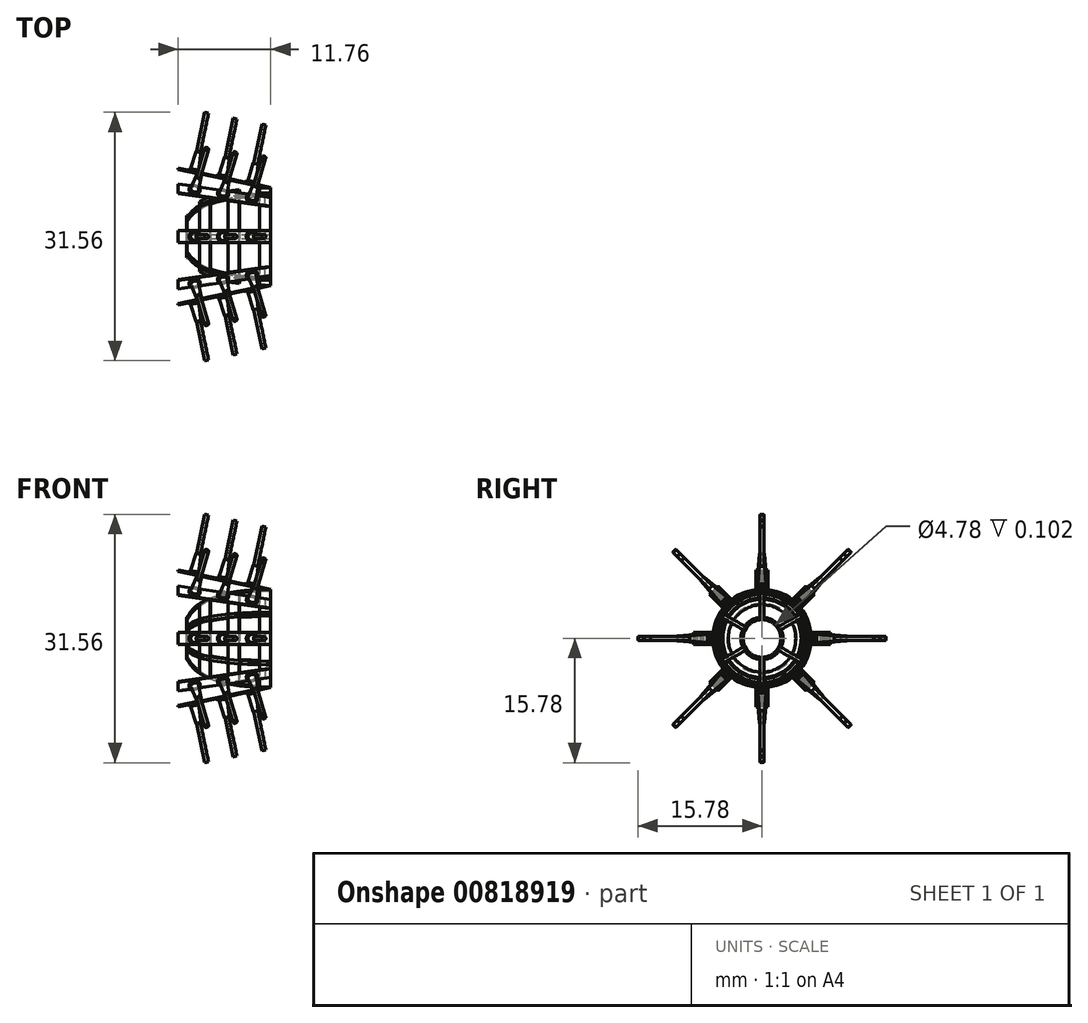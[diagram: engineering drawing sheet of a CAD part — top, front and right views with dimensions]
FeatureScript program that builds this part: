
annotation { "Feature Type Name" : "Feature", "Feature Type Description" : "" }
export const myFeature = defineFeature(function(context is Context, id is Id, definition is map)
    precondition{}
    {
        {
            var Q0;
            Q0=qCreatedBy(makeId("Front.planeOp"),FACE);
            var sketch = newSketch(context, id + "F0", { "sketchPlane" : qUnion([Q0])});
            skFitSpline(sketch, "E0", {"points": [v(0, 2.69) * mm, v(10.6, 6.24) * mm], "startDerivative": vector(4.14, 8.52) * mm, "endDerivative": vector(13.82, 0.2) * mm});
            skFitSpline(sketch, "E1", {"points": [v(0, 2.38) * mm, v(10.6, 6.06) * mm], "startDerivative": vector(4.46, 8.98) * mm, "endDerivative": vector(13.82, 0.2) * mm});
            skLineSegment(sketch, "E2", {"start": v(0, 2.69) * mm, "end": v(0, 2.38) * mm});
            skLineSegment(sketch, "E3", {"start": v(10.6, 6.24) * mm, "end": v(10.6, 6.06) * mm});
            skLineSegment(sketch, "E4", {"start": v(0, -2.69) * mm, "end": v(0, -2.38) * mm});
            skLineSegment(sketch, "E5.MirrorCS", {"start": v(10.6, -6.24) * mm, "end": v(10.6, -6.06) * mm});
            skFitSpline(sketch, "E6.MirrorCS", {"points": [v(0, -2.38) * mm, v(10.6, -6.06) * mm], "startDerivative": vector(4.46, -8.98) * mm, "endDerivative": vector(13.82, -0.2) * mm});
            skFitSpline(sketch, "E7.MirrorCS", {"points": [v(0, -2.69) * mm, v(10.6, -6.24) * mm], "startDerivative": vector(4.14, -8.52) * mm, "endDerivative": vector(13.82, -0.2) * mm});
            skLineSegment(sketch, "E8", {"start": v(0, 0) * mm, "end": v(12.51, 0) * mm, "construction": true});
            skSolve(sketch);
        }
        {
            var Q0;
            Q0=makeQuery(id+"F0.imprint","IMPRINT",FACE,{"disambiguationData":[TD([[makeQuery(id+"F0.imprint","IMPRINT",EDGE,{"derivedFrom":sQuery(id+"F0.wireOp",EDGE,"E0")}),-1.0]])]});
            var Q1;
            Q1=makeQuery(id+"F0.imprint","IMPRINT",FACE,{"disambiguationData":[TD([[makeQuery(id+"F0.imprint","IMPRINT",EDGE,{"derivedFrom":sQuery(id+"F0.wireOp",EDGE,"E4")}),-1.0]])]});
            extrude(context, id + "F1", {"entities" : qUnion([Q0, Q1]), "endBound" : BoundingType.SYMMETRIC, "depth" : 0.5 * mm, "offsetDistance" : 25.4 * mm});
        }
        {
            var Q0;
            Q0=qCreatedBy(makeId("Front.planeOp"),FACE);
            var sketch = newSketch(context, id + "F2", { "sketchPlane" : qUnion([Q0])});
            skLineSegment(sketch, "E9.bottom", {"start": v(0, 2.4) * mm, "end": v(-0.1, 2.4) * mm});
            skLineSegment(sketch, "E9.top", {"start": v(0, 2.68) * mm, "end": v(-0.1, 2.68) * mm});
            skLineSegment(sketch, "E9.left", {"start": v(0, 2.4) * mm, "end": v(0, 2.68) * mm});
            skLineSegment(sketch, "E9.right", {"start": v(-0.1, 2.4) * mm, "end": v(-0.1, 2.68) * mm});
            skLineSegment(sketch, "E10", {"start": v(0.05, 0) * mm, "end": v(4.12, 0) * mm, "construction": true});
            skSolve(sketch);
        }
        {
            var Q0;
            Q0=makeQuery(id+"F2.imprint","IMPRINT",FACE,{"disambiguationData":[TD([[makeQuery(id+"F2.imprint","IMPRINT",EDGE,{"derivedFrom":sQuery(id+"F2.wireOp",EDGE,"E9.bottom")}),-1.0]])]});
            var Q1;
            Q1=sQuery(id+"F2.wireOp",EDGE,"E10");
            revolve(context, id + "F3", {"surfaceOperationType" : NewSurfaceOperationType.NEW, "entities" : qUnion([Q0]), "axis" : qUnion([Q1]), "revolveType" : RevolveType.FULL});
        }
        {
            var Q0;
            Q0=makeQuery(id+"F1.opExtrude","SWEPT_BODY",BODY,{"disambiguationData":[OSD([sQuery(id+"F0.wireOp",EDGE,"E0"),sQuery(id+"F0.wireOp",EDGE,"E1"),sQuery(id+"F0.wireOp",EDGE,"E2"),sQuery(id+"F0.wireOp",EDGE,"E3")])]});
            var Q1;
            Q1=makeQuery(id+"F1.opExtrude","SWEPT_BODY",BODY,{"disambiguationData":[OSD([sQuery(id+"F0.wireOp",EDGE,"E4"),sQuery(id+"F0.wireOp",EDGE,"E5.MirrorCS"),sQuery(id+"F0.wireOp",EDGE,"E6.MirrorCS"),sQuery(id+"F0.wireOp",EDGE,"E7.MirrorCS")])]});
            var Q2;
            Q2=makeQuery(id+"F3.opRevolve","SWEPT_EDGE",EDGE,{"disambiguationData":[OSD([sQuery(id+"F2.wireOp",EDGE,"E9.top"),sQuery(id+"F2.wireOp",EDGE,"E9.left")])]});
            circularPattern(context, id + "F4", {"entities" : qUnion([Q0, Q1]), "axis" : qUnion([Q2]), "angle" : 360 * degree, "instanceCount" : 6, "equalSpace" : true});
        }
        {
            var Q0;
            Q0=qCreatedBy(makeId("Front.planeOp"),FACE);
            var sketch = newSketch(context, id + "F5", { "sketchPlane" : qUnion([Q0])});
            skLineSegment(sketch, "E11.bottom", {"start": v(10.59, 6.25) * mm, "end": v(9.16, 6.18) * mm});
            skLineSegment(sketch, "E11.top", {"start": v(10.6, 6.07) * mm, "end": v(9.17, 6) * mm});
            skLineSegment(sketch, "E11.left", {"start": v(10.59, 6.25) * mm, "end": v(10.6, 6.07) * mm});
            skLineSegment(sketch, "E11.right", {"start": v(9.16, 6.18) * mm, "end": v(9.17, 6) * mm});
            skLineSegment(sketch, "E12.bottom", {"start": v(6.59, 5.96) * mm, "end": v(5.17, 5.77) * mm});
            skLineSegment(sketch, "E12.top", {"start": v(6.61, 5.78) * mm, "end": v(5.2, 5.59) * mm});
            skLineSegment(sketch, "E12.left", {"start": v(6.59, 5.96) * mm, "end": v(6.61, 5.78) * mm});
            skLineSegment(sketch, "E12.right", {"start": v(5.17, 5.77) * mm, "end": v(5.2, 5.59) * mm});
            skLineSegment(sketch, "E13.bottom", {"start": v(2.9, 5.14) * mm, "end": v(1.56, 4.45) * mm});
            skLineSegment(sketch, "E13.top", {"start": v(2.98, 4.98) * mm, "end": v(1.64, 4.29) * mm});
            skLineSegment(sketch, "E13.left", {"start": v(2.9, 5.14) * mm, "end": v(2.98, 4.98) * mm});
            skLineSegment(sketch, "E13.right", {"start": v(1.56, 4.45) * mm, "end": v(1.64, 4.29) * mm});
            skLineSegment(sketch, "E14", {"start": v(0, 0) * mm, "end": v(11.03, 0) * mm, "construction": true});
            skSolve(sketch);
        }
        {
            var Q0;
            Q0=qSketchRegion(id+"F5",true);
            var Q1;
            Q1=sQuery(id+"F5.wireOp",EDGE,"E14");
            revolve(context, id + "F6", {"surfaceOperationType" : NewSurfaceOperationType.NEW, "entities" : qUnion([Q0]), "axis" : qUnion([Q1]), "revolveType" : RevolveType.FULL});
        }
        {
            var Q0;
            Q0=qCreatedBy(makeId("Front.planeOp"),FACE);
            var sketch = newSketch(context, id + "F7", { "sketchPlane" : qUnion([Q0])});
            skLineSegment(sketch, "E15", {"start": v(0, 0) * mm, "end": v(-1.16, 0) * mm, "construction": true});
            skLineSegment(sketch, "E16", {"start": v(-1.16, 0) * mm, "end": v(-1.16, 8.7) * mm, "construction": true});
            skLineSegment(sketch, "E17", {"start": v(-1.16, 8.7) * mm, "end": v(10.6, 6.24) * mm});
            skLineSegment(sketch, "E18", {"start": v(10.6, 6.24) * mm, "end": v(9.88, 6.21) * mm});
            skLineSegment(sketch, "E19", {"start": v(9.88, 6.21) * mm, "end": v(-1.16, 8.52) * mm});
            skLineSegment(sketch, "E20", {"start": v(-1.16, 8.52) * mm, "end": v(-1.16, 8.7) * mm});
            skSolve(sketch);
        }
        {
            var Q0;
            Q0=makeQuery(id+"F7.imprint","IMPRINT",FACE,{"disambiguationData":[TD([[makeQuery(id+"F7.imprint","IMPRINT",EDGE,{"derivedFrom":sQuery(id+"F7.wireOp",EDGE,"E17")}),-1.0]])]});
            extrude(context, id + "F8", {"entities" : qUnion([Q0]), "endBound" : BoundingType.SYMMETRIC, "depth" : 1.52 * mm, "offsetDistance" : 25.4 * mm});
        }
        {
            var Q0;
            Q0=makeQuery(id+"F8.opExtrude","SWEPT_BODY",BODY,{"disambiguationData":[OSD([sQuery(id+"F7.wireOp",EDGE,"E17"),sQuery(id+"F7.wireOp",EDGE,"E18"),sQuery(id+"F7.wireOp",EDGE,"E19"),sQuery(id+"F7.wireOp",EDGE,"E20")])]});
            var Q1;
            Q1=makeQuery(id+"F6.opRevolve","SWEPT_EDGE",EDGE,{"disambiguationData":[OSD([sQuery(id+"F5.wireOp",EDGE,"E11.bottom"),sQuery(id+"F5.wireOp",EDGE,"E11.right")])]});
            circularPattern(context, id + "F9", {"entities" : qUnion([Q0]), "axis" : qUnion([Q1]), "angle" : 360 * degree, "instanceCount" : 8, "equalSpace" : true});
        }
        {
            var Q0;
            Q0=qCreatedBy(makeId("Top.planeOp"),FACE);
            var sketch = newSketch(context, id + "F10", { "sketchPlane" : qUnion([Q0])});
            skLineSegment(sketch, "E21", {"start": v(1.85, -0.12) * mm, "end": v(1.85, 0.14) * mm});
            skLineSegment(sketch, "E22", {"start": v(2.6, 0.14) * mm, "end": v(1.85, 0.14) * mm});
            skLineSegment(sketch, "E23", {"start": v(5.5, -0.12) * mm, "end": v(5.5, 0.15) * mm});
            skLineSegment(sketch, "E24", {"start": v(6.25, 0.14) * mm, "end": v(5.5, 0.15) * mm});
            skLineSegment(sketch, "E25", {"start": v(9.47, -0.13) * mm, "end": v(9.47, 0.14) * mm});
            skLineSegment(sketch, "E26", {"start": v(10.21, 0.13) * mm, "end": v(9.47, 0.14) * mm});
            skLineSegment(sketch, "E27", {"start": v(1.85, -0.12) * mm, "end": v(2.6, -0.12) * mm});
            skLineSegment(sketch, "E28", {"start": v(2.6, -0.12) * mm, "end": v(2.6, 0.14) * mm});
            skLineSegment(sketch, "E29", {"start": v(5.5, -0.12) * mm, "end": v(6.26, -0.12) * mm});
            skLineSegment(sketch, "E30", {"start": v(6.26, -0.12) * mm, "end": v(6.25, 0.14) * mm});
            skLineSegment(sketch, "E31", {"start": v(9.47, -0.13) * mm, "end": v(10.2, -0.13) * mm});
            skLineSegment(sketch, "E32", {"start": v(10.2, -0.13) * mm, "end": v(10.21, 0.13) * mm});
            skSolve(sketch);
        }
        {
            var Q0;
            Q0=makeQuery(id+"F8.opExtrude","SWEPT_FACE",FACE,{"disambiguationData":[OSD([sQuery(id+"F7.wireOp",EDGE,"E17")])]});
            cPlane(context, id + "F11", {"entities" : qUnion([Q0]), "cplaneType" : CPlaneType.OFFSET, "offset" : 0 * mm, "width" : 152.4 * mm, "height" : 152.4 * mm});
        }
        {
            var Q0;
            Q0=qCreatedBy(id+"F11.planeOp",FACE);
            var sketch = newSketch(context, id + "F12", { "sketchPlane" : qUnion([Q0])});
            skCircle(sketch, "E33", {"center": v(-0.8, 0) * mm, "radius": 0.7 * mm});
            skCircle(sketch, "E34", {"center": v(2.88, 0) * mm, "radius": 0.7 * mm});
            skCircle(sketch, "E35", {"center": v(6.63, 0) * mm, "radius": 0.7 * mm});
            skSolve(sketch);
        }
        {
            var Q0;
            Q0 = qSketchRegion(id + "F12", true);
            extrude(context, id + "F13", {"entities" : qUnion([Q0]), "operationType" : NewBodyOperationType.ADD, "depth" : 0.25 * mm, "offsetDistance" : 25.4 * mm});
        }
        {
            var Q0;
            Q0=qCreatedBy(id+"F11.planeOp",FACE);
            var sketch = newSketch(context, id + "F14", { "sketchPlane" : qUnion([Q0])});
            skCircle(sketch, "E36", {"center": v(-0.8, 0) * mm, "radius": 0.52 * mm});
            skCircle(sketch, "E37", {"center": v(2.88, 0) * mm, "radius": 0.52 * mm});
            skCircle(sketch, "E38", {"center": v(6.63, 0) * mm, "radius": 0.52 * mm});
            skSolve(sketch);
        }
        {
            var Q0;
            Q0 = qSketchRegion(id + "F14", true);
            extrude(context, id + "F15", {"entities" : qUnion([Q0]), "operationType" : NewBodyOperationType.ADD, "depth" : 2.54 * mm, "offsetDistance" : 25.4 * mm});
        }
        {
            var Q0;
            Q0=makeQuery(id+"F15.opExtrude","CAP_EDGE",EDGE,{"disambiguationData":[OSD([sQuery(id+"F14.wireOp",EDGE,"E36")])],"isStart":false});
            var Q1;
            Q1=makeQuery(id+"F15.opExtrude","CAP_EDGE",EDGE,{"disambiguationData":[OSD([sQuery(id+"F14.wireOp",EDGE,"E37")])],"isStart":false});
            var Q2;
            Q2=makeQuery(id+"F15.opExtrude","CAP_EDGE",EDGE,{"disambiguationData":[OSD([sQuery(id+"F14.wireOp",EDGE,"E38")])],"isStart":false});
            chamfer(context, id + "F16", {"entities" : qUnion([Q0, Q1, Q2]), "chamferType" : ChamferType.OFFSET_ANGLE, "width" : 0.2 * mm, "oppositeDirection" : false, "angle" : 85 * degree, "tangentPropagation" : true});
        }
        {
            var Q0;
            Q0=qCreatedBy(id+"F11.planeOp",FACE);
            var sketch = newSketch(context, id + "F17", { "sketchPlane" : qUnion([Q0])});
            skCircle(sketch, "E39", {"center": v(-0.8, 0) * mm, "radius": 0.25 * mm});
            skCircle(sketch, "E40", {"center": v(2.88, 0) * mm, "radius": 0.25 * mm});
            skCircle(sketch, "E41", {"center": v(6.63, 0) * mm, "radius": 0.25 * mm});
            skSolve(sketch);
        }
        {
            var Q0;
            Q0 = qSketchRegion(id + "F17", true);
            extrude(context, id + "F18", {"entities" : qUnion([Q0]), "operationType" : NewBodyOperationType.ADD, "depth" : 7.62 * mm, "offsetDistance" : 25.4 * mm});
        }
        {
            var Q0;
            Q0=makeQuery(id+"F8.opExtrude","SWEPT_BODY",BODY,{"disambiguationData":[OSD([sQuery(id+"F7.wireOp",EDGE,"E17"),sQuery(id+"F7.wireOp",EDGE,"E18"),sQuery(id+"F7.wireOp",EDGE,"E19"),sQuery(id+"F7.wireOp",EDGE,"E20")])]});
            var Q1;
            Q1=makeQuery(id+"F6.opRevolve","SWEPT_FACE",FACE,{"disambiguationData":[OSD([sQuery(id+"F5.wireOp",EDGE,"E11.bottom")])]});
            circularPattern(context, id + "F19", {"entities" : qUnion([Q0]), "axis" : qUnion([Q1]), "angle" : 360 * degree, "instanceCount" : 8, "equalSpace" : true});
        }
    });
